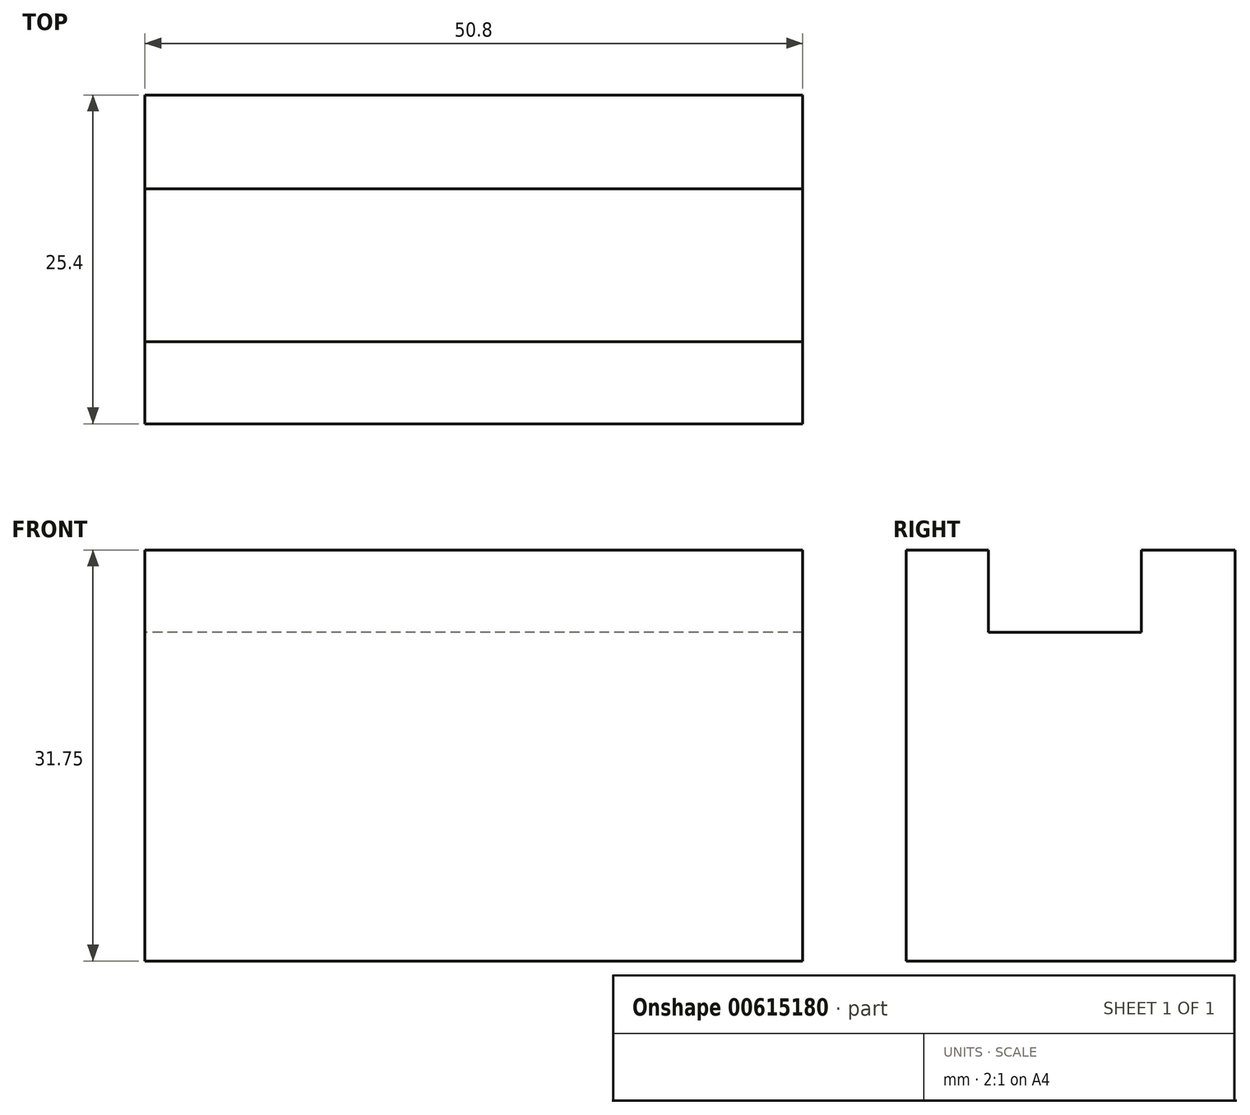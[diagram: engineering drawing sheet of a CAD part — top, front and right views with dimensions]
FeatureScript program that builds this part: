
annotation { "Feature Type Name" : "Feature", "Feature Type Description" : "" }
export const myFeature = defineFeature(function(context is Context, id is Id, definition is map)
    precondition{}
    {
        {
            var Q0;
            Q0=qCreatedBy(makeId("Right.planeOp"),FACE);
            var sketch = newSketch(context, id + "F0", { "sketchPlane" : qUnion([Q0])});
            skLineSegment(sketch, "E0", {"start": v(-25.4, 0) * mm, "end": v(0, 0) * mm});
            skLineSegment(sketch, "E1", {"start": v(0, 0) * mm, "end": v(-25.4, 0) * mm});
            skLineSegment(sketch, "E2", {"start": v(-25.4, 0) * mm, "end": v(-25.4, 31.75) * mm});
            skLineSegment(sketch, "E3", {"start": v(-25.4, 31.75) * mm, "end": v(-19.05, 31.75) * mm});
            skLineSegment(sketch, "E4", {"start": v(-19.05, 31.75) * mm, "end": v(-19.05, 25.4) * mm});
            skLineSegment(sketch, "E5", {"start": v(-19.05, 25.4) * mm, "end": v(-7.25, 25.4) * mm});
            skLineSegment(sketch, "E6", {"start": v(-7.25, 25.4) * mm, "end": v(-7.25, 31.75) * mm});
            skLineSegment(sketch, "E7", {"start": v(-7.25, 31.75) * mm, "end": v(0, 31.75) * mm});
            skLineSegment(sketch, "E8", {"start": v(0, 31.75) * mm, "end": v(0, 0) * mm});
            skSolve(sketch);
        }
        {
            var Q0;
            Q0 = qSketchRegion(id + "F0", true);
            extrude(context, id + "F1", {"entities" : qUnion([Q0]), "depth" : 25.4 * mm, "offsetDistance" : 25.4 * mm});
        }
        {
            var Q0;
            Q0=makeQuery(id+"F1.opExtrude","CAP_FACE",FACE,{"disambiguationData":[OSD([sQuery(id+"F0.wireOp",EDGE,"E1"),sQuery(id+"F0.wireOp",EDGE,"E2"),sQuery(id+"F0.wireOp",EDGE,"E3"),sQuery(id+"F0.wireOp",EDGE,"E4"),sQuery(id+"F0.wireOp",EDGE,"E5"),sQuery(id+"F0.wireOp",EDGE,"E6"),sQuery(id+"F0.wireOp",EDGE,"E7"),sQuery(id+"F0.wireOp",EDGE,"E8")])],"isStart":false});
            extrude(context, id + "F2", {"entities" : qUnion([Q0]), "operationType" : NewBodyOperationType.ADD, "depth" : 25.4 * mm, "offsetDistance" : 25.4 * mm});
        }
    });
